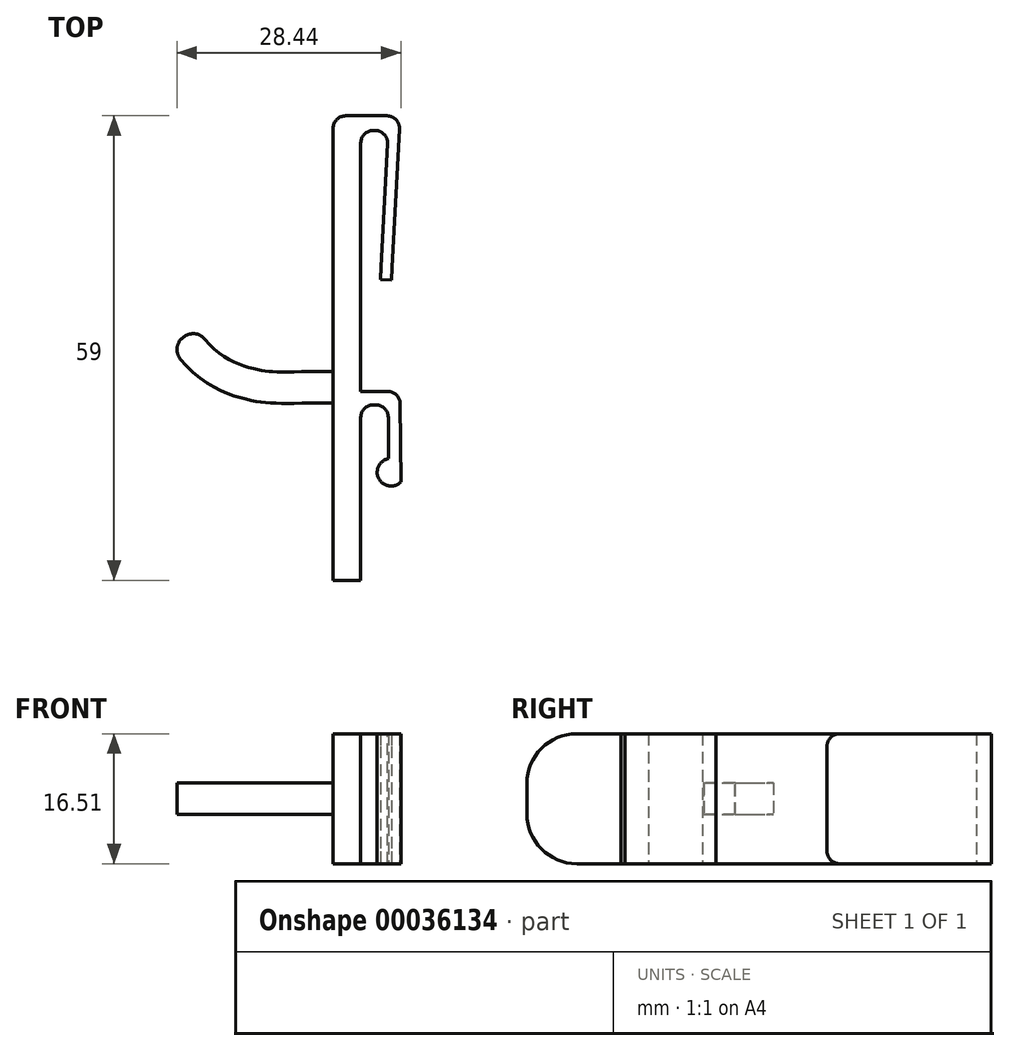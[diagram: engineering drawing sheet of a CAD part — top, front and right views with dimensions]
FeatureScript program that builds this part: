
annotation { "Feature Type Name" : "Feature", "Feature Type Description" : "" }
export const myFeature = defineFeature(function(context is Context, id is Id, definition is map)
    precondition{}
    {
        {
            var Q0;
            Q0=qCreatedBy(makeId("Top.planeOp"),FACE);
            var sketch = newSketch(context, id + "F0", { "sketchPlane" : qUnion([Q0])});
            skLineSegment(sketch, "E0.bottom", {"start": v(-5, 29.5) * mm, "end": v(3.5, 29.5) * mm});
            skLineSegment(sketch, "E0.top", {"start": v(-5, -29.5) * mm, "end": v(3.5, -29.5) * mm});
            skLineSegment(sketch, "E0.left", {"start": v(-5, 29.5) * mm, "end": v(-5, -29.5) * mm});
            skLineSegment(sketch, "E0.right", {"start": v(3.5, 29.5) * mm, "end": v(3.5, -29.5) * mm});
            skLineSegment(sketch, "E1", {"start": v(-1.5, -29.5) * mm, "end": v(-1.5, 27.64) * mm});
            skLineSegment(sketch, "E2", {"start": v(-1.5, 27.64) * mm, "end": v(2, 27.64) * mm});
            skLineSegment(sketch, "E3", {"start": v(2, 27.64) * mm, "end": v(2, 8.9) * mm});
            skLineSegment(sketch, "E4", {"start": v(2, 8.9) * mm, "end": v(3.5, 8.9) * mm});
            skLineSegment(sketch, "E5", {"start": v(-1.5, -5.5) * mm, "end": v(3.5, -5.5) * mm});
            skLineSegment(sketch, "E6", {"start": v(-1.5, -7.2) * mm, "end": v(2, -7.2) * mm});
            skLineSegment(sketch, "E7", {"start": v(2, -7.2) * mm, "end": v(2, -17.5) * mm});
            skLineSegment(sketch, "E8", {"start": v(2, -17.5) * mm, "end": v(3.5, -17.5) * mm});
            skCircle(sketch, "E9", {"center": v(2.33, -15.78) * mm, "radius": 1.75 * mm});
            skLineSegment(sketch, "E10", {"start": v(-5, 1.5) * mm, "end": v(-24, 1.5) * mm});
            skLineSegment(sketch, "E11", {"start": v(-24, 1.5) * mm, "end": v(-24, -10.5) * mm});
            skLineSegment(sketch, "E12", {"start": v(-24, -10.5) * mm, "end": v(-5, -10.5) * mm});
            skLineSegment(sketch, "E13", {"start": v(-5, -5) * mm, "end": v(-10.87, -5) * mm});
            skLineSegment(sketch, "E14", {"start": v(-10.87, -5) * mm, "end": v(-18.73, -2.9) * mm});
            skLineSegment(sketch, "E15", {"start": v(-18.73, -2.9) * mm, "end": v(-24, 1.5) * mm});
            skSolve(sketch);
        }
        {
            var Q0;
            Q0=qCreatedBy(makeId("Top.planeOp"),FACE);
            var sketch = newSketch(context, id + "F1", { "sketchPlane" : qUnion([Q0])});
            skLineSegment(sketch, "E16.0", {"start": v(-5, 29.5) * mm, "end": v(3.5, 29.5) * mm});
            skLineSegment(sketch, "E16.1", {"start": v(-5, -29.5) * mm, "end": v(3.5, -29.5) * mm});
            skLineSegment(sketch, "E16.2", {"start": v(-5, 29.5) * mm, "end": v(-5, -29.5) * mm});
            skLineSegment(sketch, "E16.4", {"start": v(-1.5, -29.5) * mm, "end": v(-1.5, -7.2) * mm});
            skLineSegment(sketch, "E16.5", {"start": v(-1.5, 27.64) * mm, "end": v(2, 27.64) * mm});
            skLineSegment(sketch, "E16.8", {"start": v(-1.5, -5.5) * mm, "end": v(3.5, -5.5) * mm});
            skLineSegment(sketch, "E16.9", {"start": v(-1.5, -7.2) * mm, "end": v(2, -7.2) * mm});
            skLineSegment(sketch, "E16.10", {"start": v(2, -7.2) * mm, "end": v(2, -14.06) * mm});
            skArc(sketch, "E16.12", {"start": v(2, -14.06) * mm, "mid": v(0.8, -16.62) * mm, "end": v(3.6, -17) * mm});
            skPoint(sketch, "E17.orphan", {"position": v(3.5, -29.5) * mm});
            skPoint(sketch, "E18.orphan", {"position": v(3.5, -17.5) * mm});
            skPoint(sketch, "E16.11.start.orphan", {"position": v(2, -17.5) * mm});
            skLineSegment(sketch, "E19.trimOffspring", {"start": v(-1.5, -5.5) * mm, "end": v(-1.5, 27.64) * mm});
            skLineSegment(sketch, "E20.trimOffspring", {"start": v(3.5, -5.5) * mm, "end": v(3.6, -17) * mm});
            skPoint(sketch, "E16.6.end.orphan", {"position": v(2, 8.9) * mm});
            skPoint(sketch, "E16.6.start.orphan", {"position": v(2, 27.64) * mm});
            skPoint(sketch, "E16.3.start.orphan", {"position": v(3.5, 29.5) * mm});
            skPoint(sketch, "E16.7.end.orphan", {"position": v(3.5, 8.9) * mm});
            skPoint(sketch, "E16.7.start.orphan", {"position": v(2, 8.9) * mm});
            skLineSegment(sketch, "E21", {"start": v(2, 27.64) * mm, "end": v(1, 8.7) * mm});
            skLineSegment(sketch, "E22", {"start": v(3.5, 29.5) * mm, "end": v(2.4, 8.63) * mm});
            skLineSegment(sketch, "E23", {"start": v(2.4, 8.63) * mm, "end": v(1, 8.7) * mm});
            skSolve(sketch);
        }
        {
            var Q0;
            Q0 = qSketchRegion(id + "F1", true);
            extrude(context, id + "F2", {"entities" : qUnion([Q0]), "depth" : 8.25 * mm, "hasSecondDirection" : true, "secondDirectionOppositeDirection" : true, "secondDirectionDepth" : 8.25 * mm});
        }
        {
            var Q0;
            Q0=qCreatedBy(makeId("Top.planeOp"),FACE);
            var sketch = newSketch(context, id + "F3", { "sketchPlane" : qUnion([Q0])});
            skFitSpline(sketch, "E24", {"points": [v(-5, -5) * mm, v(-15.1, -4.68) * mm, v(-23.93, 1.45) * mm], "startDerivative": vector(-40.1, 0) * mm, "endDerivative": vector(-14.64, 25.42) * mm});
            skSolve(sketch);
        }
        {
            var Q0;
            Q0=makeQuery(id+"F2.opExtrude","SWEPT_FACE",FACE,{"disambiguationData":[OSD([sQuery(id+"F1.wireOp",EDGE,"E16.2")])]});
            var sketch = newSketch(context, id + "F4", { "sketchPlane" : qUnion([Q0])});
            skLineSegment(sketch, "E25.bottom", {"start": v(3, -2) * mm, "end": v(7, -2) * mm});
            skLineSegment(sketch, "E25.top", {"start": v(3, 2) * mm, "end": v(7, 2) * mm});
            skLineSegment(sketch, "E25.left", {"start": v(3, -2) * mm, "end": v(3, 2) * mm});
            skLineSegment(sketch, "E25.right", {"start": v(7, -2) * mm, "end": v(7, 2) * mm});
            skLineSegment(sketch, "E26", {"start": v(5, -2) * mm, "end": v(5, 2) * mm, "construction": true});
            skSolve(sketch);
        }
        {
            var Q0;
            Q0 = qSketchRegion(id + "F4", true);
            var Q1;
            Q1 = qConstructionFilter(qBodyType(qCreatedBy(id + "F3" ,EDGE), BodyType.WIRE), ConstructionObject.NO);
            sweep(context, id + "F5", {"operationType" : NewBodyOperationType.ADD, "profiles" : qUnion([Q0]), "path" : qUnion([Q1])});
        }
        {
            var Q0;
            Q0=makeQuery(id+"F5.opSweep","CAP_EDGE",EDGE,{"disambiguationData":[OSD([sQuery(id+"F3.wireOp",VERTEX,"E24.end"),sQuery(id+"F4.wireOp",EDGE,"E25.left")])],"isStart":false});
            var Q1;
            Q1=makeQuery(id+"F5.opSweep","CAP_EDGE",EDGE,{"disambiguationData":[OSD([sQuery(id+"F3.wireOp",VERTEX,"E24.end"),sQuery(id+"F4.wireOp",EDGE,"E25.right")])],"isStart":false});
            fillet(context, id + "F6", {"entities" : qUnion([Q0, Q1]), "radius" : 1.9 * mm, "tangentPropagation" : true, "allowEdgeOverflow" : false});
        }
        {
            var Q0;
            Q0=makeQuery(id+"F2.opExtrude","CAP_EDGE",EDGE,{"disambiguationData":[OSD([sQuery(id+"F1.wireOp",EDGE,"E16.1")])],"isStart":false});
            var Q1;
            Q1=makeQuery(id+"F2.opExtrude","CAP_EDGE",EDGE,{"disambiguationData":[OSD([sQuery(id+"F1.wireOp",EDGE,"E16.1")])],"isStart":true});
            fillet(context, id + "F7", {"entities" : qUnion([Q0, Q1]), "radius" : 6.35 * mm, "tangentPropagation" : true, "allowEdgeOverflow" : false});
        }
        {
            var Q0;
            Q0=makeQuery(id+"F2.opExtrude","SWEPT_EDGE",EDGE,{"disambiguationData":[OSD([sQuery(id+"F1.wireOp",EDGE,"E16.0"),sQuery(id+"F1.wireOp",EDGE,"E22")])]});
            var Q1;
            Q1=makeQuery(id+"F2.opExtrude","SWEPT_EDGE",EDGE,{"disambiguationData":[OSD([sQuery(id+"F1.wireOp",EDGE,"E16.0"),sQuery(id+"F1.wireOp",EDGE,"E16.2")])]});
            var Q2;
            Q2=makeQuery(id+"F2.opExtrude","SWEPT_EDGE",EDGE,{"disambiguationData":[OSD([sQuery(id+"F1.wireOp",EDGE,"E16.8"),sQuery(id+"F1.wireOp",EDGE,"E20.trimOffspring")])]});
            var Q3;
            Q3=makeQuery(id+"F2.opExtrude","SWEPT_EDGE",EDGE,{"disambiguationData":[OSD([sQuery(id+"F1.wireOp",EDGE,"E16.5"),sQuery(id+"F1.wireOp",EDGE,"E19.trimOffspring")])]});
            var Q4;
            Q4=makeQuery(id+"F2.opExtrude","SWEPT_EDGE",EDGE,{"disambiguationData":[OSD([sQuery(id+"F1.wireOp",EDGE,"E16.5"),sQuery(id+"F1.wireOp",EDGE,"E21")])]});
            var Q5;
            Q5=makeQuery(id+"F2.opExtrude","SWEPT_EDGE",EDGE,{"disambiguationData":[OSD([sQuery(id+"F1.wireOp",EDGE,"E16.9"),sQuery(id+"F1.wireOp",EDGE,"E16.10")])]});
            var Q6;
            Q6=makeQuery(id+"F2.opExtrude","SWEPT_EDGE",EDGE,{"disambiguationData":[OSD([sQuery(id+"F1.wireOp",EDGE,"E16.4"),sQuery(id+"F1.wireOp",EDGE,"E16.9")])]});
            var Q7;
            Q7=makeQuery(id+"F2.opExtrude","CAP_EDGE",EDGE,{"disambiguationData":[OSD([sQuery(id+"F1.wireOp",EDGE,"E23")])],"isStart":false});
            var Q8;
            Q8=makeQuery(id+"F2.opExtrude","CAP_EDGE",EDGE,{"disambiguationData":[OSD([sQuery(id+"F1.wireOp",EDGE,"E23")])],"isStart":true});
            fillet(context, id + "F8", {"entities" : qUnion([Q0, Q1, Q2, Q3, Q4, Q5, Q6, Q7, Q8]), "radius" : 1.59 * mm, "tangentPropagation" : true, "allowEdgeOverflow" : false});
        }
    });
